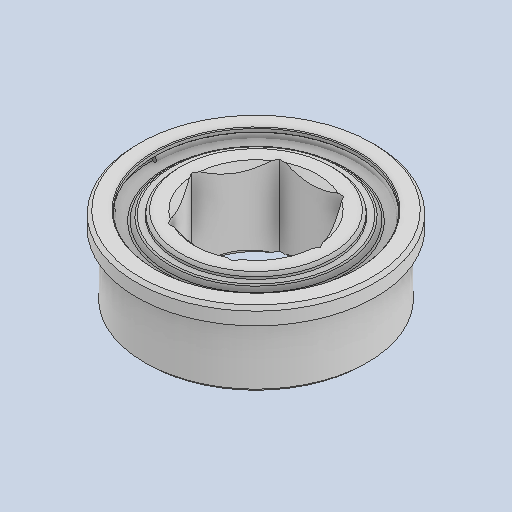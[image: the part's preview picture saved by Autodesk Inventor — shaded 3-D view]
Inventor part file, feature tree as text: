
AUTODESK INVENTOR PART (.ipt)
format: ipt  version: 2023 (Build 270158000, 158)  size: 306,176 bytes
history: native  units: in
note: dims shown in document units (in); Inventor stores cm internally (conversion verified against a paired STEP export)
features: mirror x2, revolve x1
ambient origin geometry x8: Origin, YZ Plane, XZ Plane, XY Plane, X Axis, Y Axis, Z Axis, Center Point
bodies: Solid1 (feature_tree), Solid2 (feature_tree), Solid3 (feature_tree)
feature tree (3):
  revolve  "Revolve1"  [1 undecoded]
  mirror  "Mirror3"
  mirror  "Mirror5"
note: 1 required parameter value undecoded (feature->parameter linkage not recoverable at this tier; creation-order binding heuristic only, values carry confidence <= 0.55)
